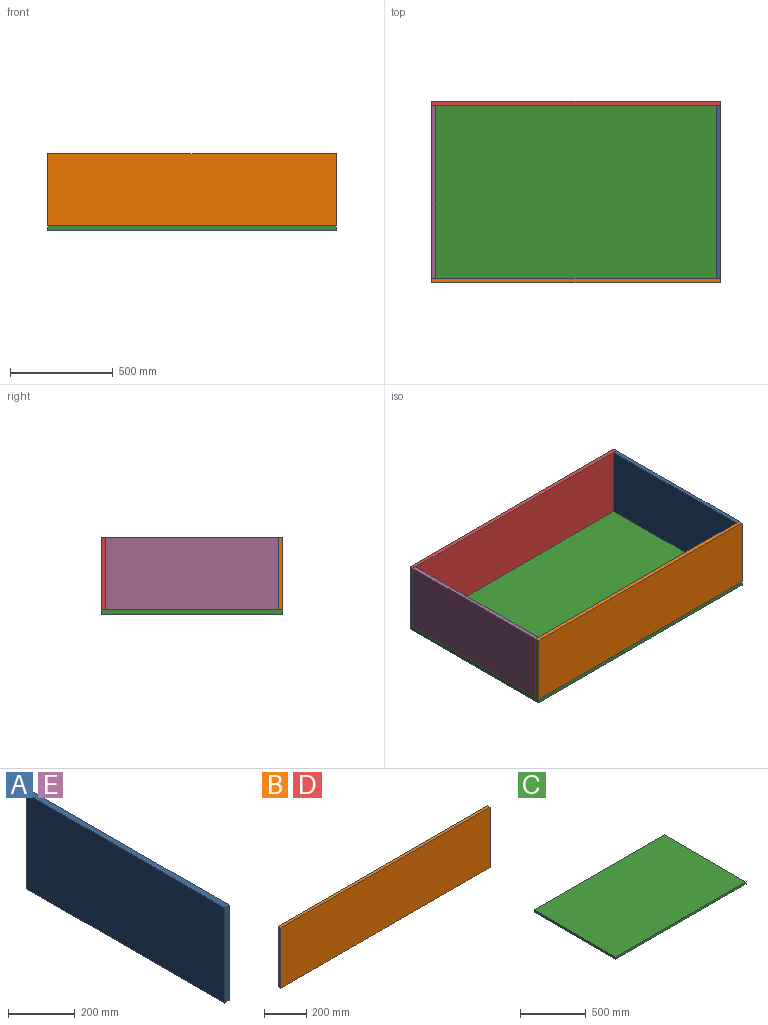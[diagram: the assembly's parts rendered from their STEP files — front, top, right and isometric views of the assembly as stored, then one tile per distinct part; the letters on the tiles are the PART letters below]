
ASSEMBLY  parts=5 mates=13
PART A: 6 faces, bbox 20x840x350 mm
  f0: plane 350x20mm, normal (0,-1,0), area 7000mm2, adj f1,f3,f4,f5
  f1: plane 840x20mm, normal (0,0,-1), area 16800mm2, adj f0,f2,f4,f5
  f2: plane 350x20mm, normal (0,1,0), area 7000mm2, adj f1,f3,f4,f5
  f3: plane 840x20mm, normal (0,0,1), area 16800mm2, adj f0,f2,f4,f5
  f4: plane 840x350mm, normal (1,0,0), area 294000mm2, adj f0,f1,f2,f3
  f5: plane 840x350mm, normal (-1,0,0), area 294000mm2, adj f0,f1,f2,f3
PART B: 6 faces, bbox 1400x20x350 mm
  f0: plane 350x20mm, normal (-1,0,0), area 7000mm2, adj f1,f3,f4,f5
  f1: plane 1400x20mm, normal (0,0,-1), area 28000mm2, adj f0,f2,f4,f5
  f2: plane 350x20mm, normal (1,0,0), area 7000mm2, adj f1,f3,f4,f5
  f3: plane 1400x20mm, normal (0,0,1), area 28000mm2, adj f0,f2,f4,f5
  f4: plane 1400x350mm, normal (0,-1,0), area 490000mm2, adj f0,f1,f2,f3
  f5: plane 1400x350mm, normal (0,1,0), area 490000mm2, adj f0,f1,f2,f3
PART C: 6 faces, bbox 1400x880x20 mm
  f0: plane 880x20mm, normal (-1,0,0), area 17600mm2, adj f1,f3,f4,f5
  f1: plane 1400x20mm, normal (0,-1,0), area 28000mm2, adj f0,f2,f4,f5
  f2: plane 880x20mm, normal (1,0,0), area 17600mm2, adj f1,f3,f4,f5
  f3: plane 1400x20mm, normal (0,1,0), area 28000mm2, adj f0,f2,f4,f5
  f4: plane 1400x880mm, normal (0,0,1), area 1232000mm2, adj f0,f1,f2,f3
  f5: plane 1400x880mm, normal (0,0,-1), area 1232000mm2, adj f0,f1,f2,f3
PART D: same geometry as B
PART E: same geometry as A
PLACE A t=(689.93,-407.36,20)mm
PLACE B t=(-690.07,-407.36,20)mm
PLACE C rot(axis=(0,0,1),180deg) t=(709.93,452.64,0)mm
PLACE D t=(-690.07,452.64,20)mm
PLACE E t=(-690.07,-407.36,20)mm
MATE planar D.f5 <-> C.f1  axis (0,1,0) through (9.93,452.64,20)mm
MATE planar A.f4 <-> B.f2  axis (1,0,0) through (709.93,-407.36,195)mm
MATE planar B.f4 <-> C.f3  axis (0,-1,0) through (9.93,-427.36,20)mm
MATE planar C.f4 <-> A.f1  axis (0,0,1) through (709.93,12.64,20)mm
MATE planar B.f5 <-> A.f0  axis (0,1,0) through (709.93,-407.36,195)mm
MATE planar A.f3 <-> D.f3  axis (0,0,1) through (709.93,432.64,370)mm
MATE planar A.f4 <-> D.f2  axis (1,0,0) through (709.93,432.64,195)mm
MATE planar B.f4 <-> C.f3  axis (0,-1,0) through (9.93,-427.36,20)mm
MATE planar E.f5 <-> B.f0  axis (-1,0,0) through (-690.07,-407.36,195)mm
MATE planar A.f0 <-> E.f0  axis (0,-1,0) through (699.93,-407.36,195)mm
MATE planar B.f3 <-> A.f3  axis (0,0,1) through (709.93,-407.36,370)mm
MATE planar C.f2 <-> E.f5  axis (-1,0,0) through (-690.07,12.64,20)mm
MATE planar C.f4 <-> E.f1  axis (0,0,1) through (-690.07,12.64,20)mm
